# Revit family: KEUCO_14901010600
name_source: partatom
category: Allgemeines Modell
revit_build: Autodesk Revit 2016 (Build: 20150220_1215(x64)
units: mm (PartAtom-declared; Revit-internal decimal feet)

## family parameters
Arbeitsebenenbasiert = Ja
Beim Laden mit Abzugskörper schneiden = Nein
Bemaßung runder Anschluss = Durchmesser verwenden
Gemeinsam genutzt = Nein
Immer vertikal = Nein
Kann Basisbauteil für Bewehrung sein = Nein
Raumberechnungspunkt = Nein
Teiletyp = Normal

## types (6) — shared parameters
Beschreibung = --
Hersteller = KEUCO
Serie = Plan
URL = https://www.keuco.com
Vorgabe-Ansicht = 1219 mm
zero-valued in all types: Gewicht

## per-type parameters (varying)
| type | Ausschreibungstext | Baugruppenkennzeichen | Rail Length | Stange Material |
| 14901010600 | KEUCO PLAN Badetuchhalter 14901010600
Hochglanzverchromter Badetuchhalter in ästhetischem, funktionalem Design
antistatisch, leicht zu reinigen
Achsmaß 600 mm, bei einer Gesamtbreite von 651 mm
Ausladung 67 mm
Der Badetuchhalter wird verdeckt angebracht
Lieferung inkl. korrosionsfreiem Befestigungsmaterial |  | 651 mm  [stored 2.13583 ft] | verchromt |
| 14901010800 | KEUCO PLAN Badetuchhalter 14901010800
Hochglanzverchromter Badetuchhalter in ästhetischem, funktionalem Design
antistatisch, leicht zu reinigen
Achsmaß 800 mm, bei einer Gesamtbreite von 851 mm
Ausladung 67 mm
Der Badetuchhalter wird verdeckt angebracht
Lieferung inkl. korrosionsfreiem Befestigungsmaterial |  | 851 mm  [stored 2.79199 ft] | verchromt |
| 14901070600 | KEUCO PLAN Badetuchhalter 14901070600
Badetuchhalter mit Halteelement aus hochwertigem Edelstahl 
in ästhetischem, funktionalem Design
antistatisch, leicht zu reinigen
Achsmaß 600 mm, bei einer Gesamtbreite von 651 mm
Ausladung 67 mm
Der Badetuchhalter wird verdeckt angebracht
Lieferung inkl. korrosionsfreiem Befestigungsmaterial | Hochglanzverchromter Badetuchhalter in ästhetischem, funktionalem Design
antistatisch, leicht zu reinigen
Achsmaß 800 mm, bei einer Gesamtbreite von 851 mm
Ausladung 67 mm
Der Badetuchhalter wird verdeckt angebracht
Lieferung inkl. korrosionsfreiem Befestigungsmaterial | 651 mm  [stored 2.13583 ft] | Edelstahl |
| 14901070800 | KEUCO PLAN Badetuchhalter 14901070800
Badetuchhalter mit Halteelement aus hochwertigem Edelstahl 
in ästhetischem, funktionalem Design
antistatisch, leicht zu reinigen
Achsmaß 800 mm, bei einer Gesamtbreite von 851 mm
Ausladung 67 mm
Der Badetuchhalter wird verdeckt angebracht
Lieferung inkl. korrosionsfreiem Befestigungsmaterial |  | 851 mm  [stored 2.79199 ft] | Edelstahl |
| 14901170600 | KEUCO PLAN Badetuchhalter 14901170600
Eleganter Badetuchhalter mit Halteelementen 
aus silber-eloxiertem Aluminium (E6 EV1)/verchromt 
in ästhetischem, funktionalem Design
antistatisch, leicht zu reinigen
Die Wandhalterungen sind als Design-Element hochglanzverchromt
Achsmaß 600 mm, bei einer Gesamtbreite von 651 mm
Ausladung 67 mm
Der Badetuchhalter wird verdeckt angebracht
Lieferung inkl. korrosionsfreiem Befestigungsmaterial |  | 651 mm  [stored 2.13583 ft] | Aluminium silber-eloxiert (E6 EV1) |
| 14901170800 | KEUCO PLAN Badetuchhalter 14901170800
Eleganter Badetuchhalter mit Halteelementen
aus silber-eloxiertem Aluminium (E6 EV1)/verchromt 
in ästhetischem, funktionalem Design, 
antistatisch, leicht zu reinigen
Die Wandhalterungen sind als Design-Element hochglanzverchromt
Achsmaß 800 mm, bei einer Gesamtbreite von 851 mm
Ausladung 67 mm
Der Badetuchhalter wird verdeckt angebracht
Lieferung inkl. korrosionsfreiem Befestigungsmaterial |  | 851 mm  [stored 2.79199 ft] | Aluminium silber-eloxiert (E6 EV1) |

note: column(s) folded — value = type name in every type: Artikelnummer

note: [stored X ft] marks values corroborated as IEEE doubles in the binary element streams (Revit-internal decimal feet)

## geometry (parser evidence)
native form markers: Blend x9, Sweep x3
no freeform markers — native parametric forms only
